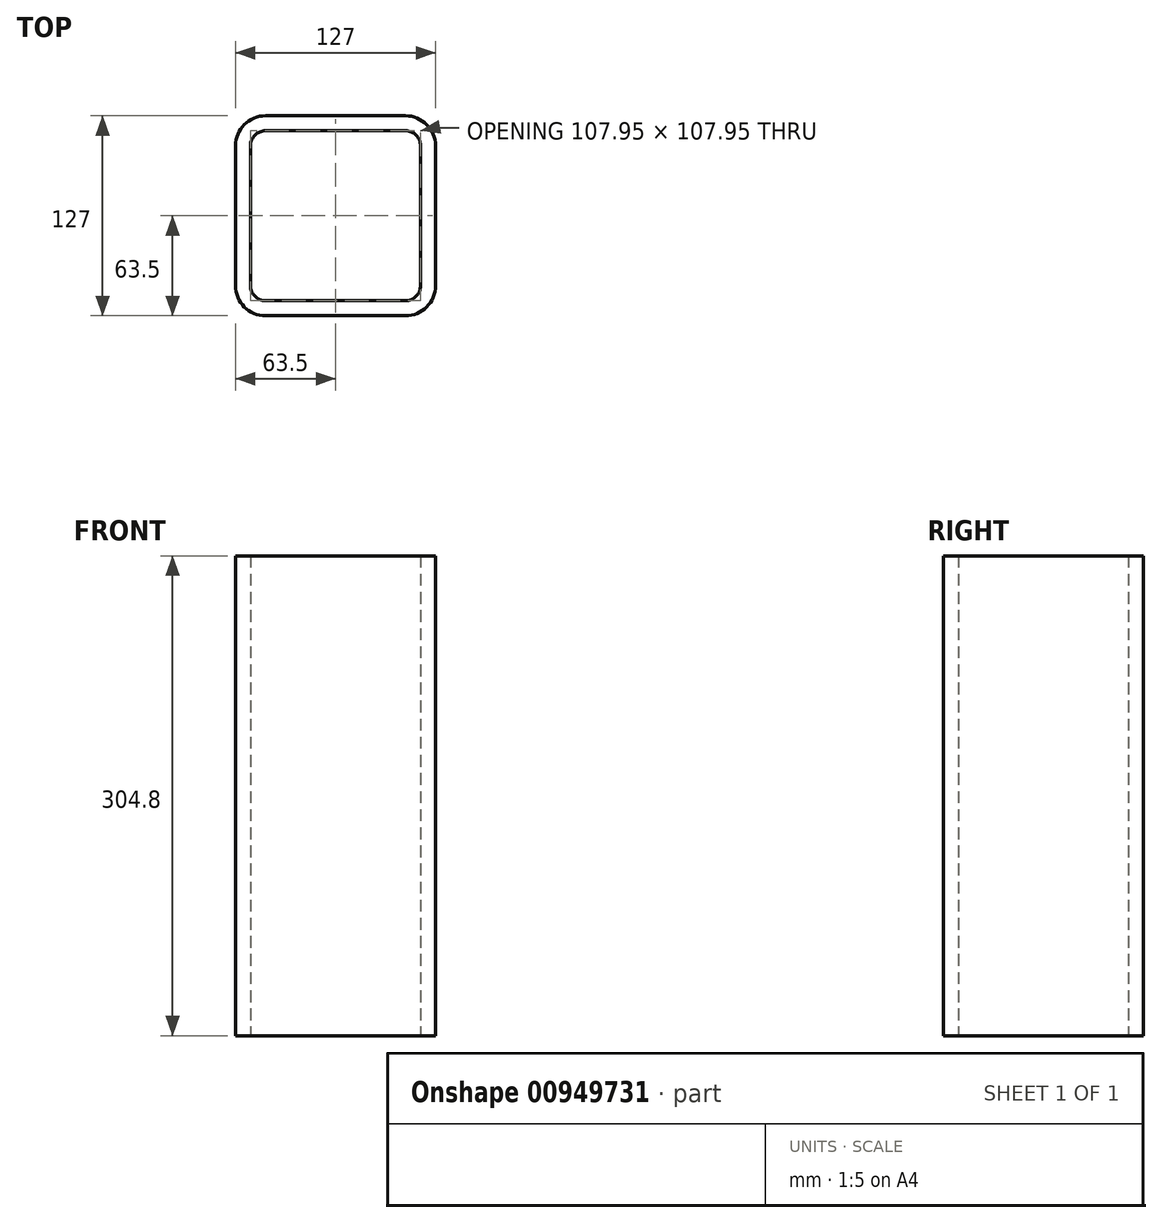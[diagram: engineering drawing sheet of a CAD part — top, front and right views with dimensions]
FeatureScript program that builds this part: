
annotation { "Feature Type Name" : "Feature", "Feature Type Description" : "" }
export const myFeature = defineFeature(function(context is Context, id is Id, definition is map)
    precondition{}
    {
        {
            var Q0;
            Q0=qCreatedBy(makeId("Top.planeOp"),FACE);
            var sketch = newSketch(context, id + "F0", { "sketchPlane" : qUnion([Q0])});
            skLineSegment(sketch, "E0.bottom", {"start": v(-44.45, -63.5) * mm, "end": v(44.45, -63.5) * mm});
            skLineSegment(sketch, "E0.top", {"start": v(-44.45, 63.5) * mm, "end": v(44.45, 63.5) * mm});
            skLineSegment(sketch, "E0.left", {"start": v(-63.5, -44.45) * mm, "end": v(-63.5, 44.45) * mm});
            skLineSegment(sketch, "E0.right", {"start": v(63.5, -44.45) * mm, "end": v(63.5, 44.45) * mm});
            skPoint(sketch, "E0.middle", {"position": v(0, 0) * mm});
            skLineSegment(sketch, "E1.bottom", {"start": v(-44.45, -53.97) * mm, "end": v(44.45, -53.97) * mm});
            skLineSegment(sketch, "E1.top", {"start": v(-44.45, 53.97) * mm, "end": v(44.45, 53.97) * mm});
            skLineSegment(sketch, "E1.left", {"start": v(-53.97, -44.45) * mm, "end": v(-53.97, 44.45) * mm});
            skLineSegment(sketch, "E1.right", {"start": v(53.97, -44.45) * mm, "end": v(53.97, 44.45) * mm});
            skPoint(sketch, "E2.visualSharp", {"position": v(-63.5, -63.5) * mm});
            skArc(sketch, "E2.filletArc", {"start": v(-63.5, -44.45) * mm, "mid": v(-57.92, -57.92) * mm, "end": v(-44.45, -63.5) * mm});
            skPoint(sketch, "E3.visualSharp", {"position": v(63.5, -63.5) * mm});
            skArc(sketch, "E3.filletArc", {"start": v(44.45, -63.5) * mm, "mid": v(57.92, -57.92) * mm, "end": v(63.5, -44.45) * mm});
            skPoint(sketch, "E4.visualSharp", {"position": v(63.5, 63.5) * mm});
            skArc(sketch, "E4.filletArc", {"start": v(63.5, 44.45) * mm, "mid": v(57.92, 57.92) * mm, "end": v(44.45, 63.5) * mm});
            skPoint(sketch, "E5.visualSharp", {"position": v(-63.5, 63.5) * mm});
            skArc(sketch, "E5.filletArc", {"start": v(-44.45, 63.5) * mm, "mid": v(-57.92, 57.92) * mm, "end": v(-63.5, 44.45) * mm});
            skPoint(sketch, "E6.visualSharp", {"position": v(-53.97, 53.97) * mm});
            skArc(sketch, "E6.filletArc", {"start": v(-44.45, 53.97) * mm, "mid": v(-51.19, 51.19) * mm, "end": v(-53.97, 44.45) * mm});
            skPoint(sketch, "E7.visualSharp", {"position": v(-53.97, -53.97) * mm});
            skArc(sketch, "E7.filletArc", {"start": v(-53.97, -44.45) * mm, "mid": v(-51.19, -51.19) * mm, "end": v(-44.45, -53.97) * mm});
            skPoint(sketch, "E8.visualSharp", {"position": v(53.97, -53.97) * mm});
            skArc(sketch, "E8.filletArc", {"start": v(44.45, -53.97) * mm, "mid": v(51.19, -51.19) * mm, "end": v(53.97, -44.45) * mm});
            skPoint(sketch, "E9.visualSharp", {"position": v(53.97, 53.97) * mm});
            skArc(sketch, "E9.filletArc", {"start": v(53.97, 44.45) * mm, "mid": v(51.19, 51.19) * mm, "end": v(44.45, 53.97) * mm});
            skSolve(sketch);
        }
        {
            var Q0;
            Q0 = qSketchRegion(id + "F0", true);
            extrude(context, id + "F1", {"entities" : qUnion([Q0]), "depth" : 304.8 * mm, "offsetDistance" : 25.4 * mm});
        }
    });
